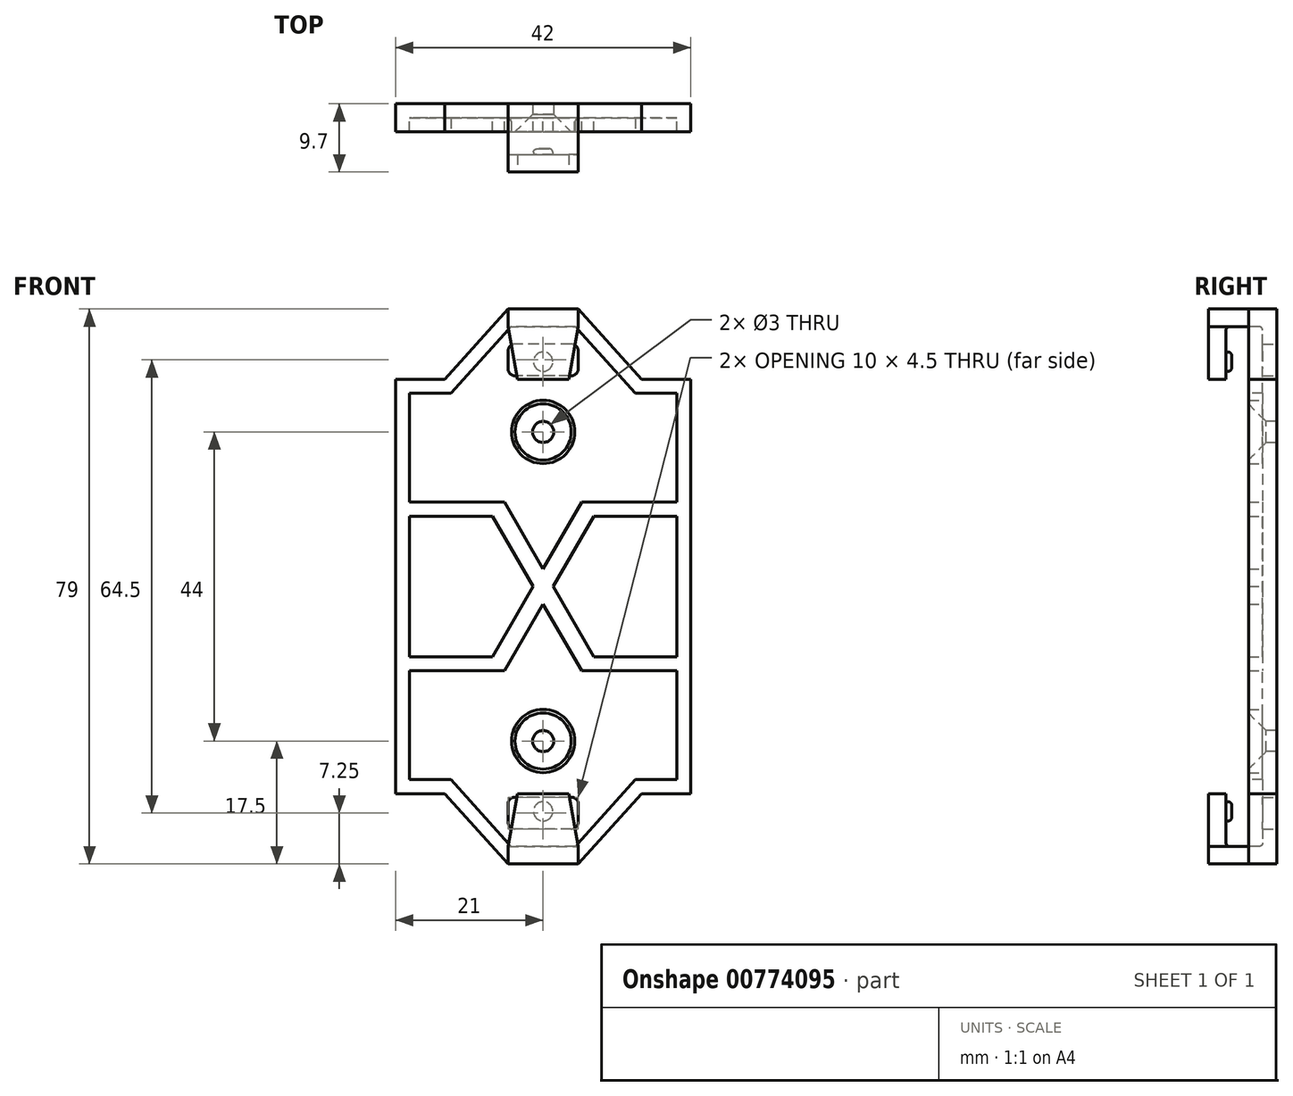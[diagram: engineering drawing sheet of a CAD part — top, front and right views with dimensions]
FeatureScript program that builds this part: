
annotation { "Feature Type Name" : "Feature", "Feature Type Description" : "" }
export const myFeature = defineFeature(function(context is Context, id is Id, definition is map)
    precondition{}
    {
        {
            var Q0;
            Q0=qCreatedBy(makeId("Front.planeOp"),FACE);
            var sketch = newSketch(context, id + "F0", { "sketchPlane" : qUnion([Q0])});
            skLineSegment(sketch, "E0.bottom", {"start": v(-21, 29.5) * mm, "end": v(-14, 29.5) * mm});
            skLineSegment(sketch, "E0.top", {"start": v(-21, -29.5) * mm, "end": v(-14, -29.5) * mm});
            skLineSegment(sketch, "E0.left", {"start": v(-21, 29.5) * mm, "end": v(-21, -29.5) * mm});
            skLineSegment(sketch, "E0.right", {"start": v(21, 29.5) * mm, "end": v(21, -29.5) * mm});
            skLineSegment(sketch, "E1", {"start": v(-14, 29.5) * mm, "end": v(-5, 39.5) * mm});
            skLineSegment(sketch, "E2", {"start": v(-5, 39.5) * mm, "end": v(5, 39.5) * mm});
            skLineSegment(sketch, "E3", {"start": v(5, 39.5) * mm, "end": v(14, 29.5) * mm});
            skLineSegment(sketch, "E4", {"start": v(0, 66.84) * mm, "end": v(0, -52.22) * mm, "construction": true});
            skLineSegment(sketch, "E5.trimOffspring", {"start": v(14, 29.5) * mm, "end": v(21, 29.5) * mm});
            skLineSegment(sketch, "E6", {"start": v(-14, -29.5) * mm, "end": v(-5, -39.5) * mm});
            skLineSegment(sketch, "E7", {"start": v(-5, -39.5) * mm, "end": v(5, -39.5) * mm});
            skLineSegment(sketch, "E8", {"start": v(5, -39.5) * mm, "end": v(14, -29.5) * mm});
            skLineSegment(sketch, "E9.trimOffspring", {"start": v(14, -29.5) * mm, "end": v(21, -29.5) * mm});
            skLineSegment(sketch, "E10", {"start": v(-46.22, 0) * mm, "end": v(54.83, 0) * mm, "construction": true});
            skSolve(sketch);
        }
        {
            var Q0;
            Q0 = qSketchRegion(id + "F0", true);
            extrude(context, id + "F1", {"entities" : qUnion([Q0]), "oppositeDirection" : true, "depth" : 4 * mm, "offsetDistance" : 25 * mm});
        }
        {
            var Q0;
            Q0=makeQuery(id+"F1.opExtrude","CAP_FACE",FACE,{"disambiguationData":[OSD([sQuery(id+"F0.wireOp",EDGE,"E0.bottom"),sQuery(id+"F0.wireOp",EDGE,"E0.top"),sQuery(id+"F0.wireOp",EDGE,"E0.left"),sQuery(id+"F0.wireOp",EDGE,"E0.right"),sQuery(id+"F0.wireOp",EDGE,"E1"),sQuery(id+"F0.wireOp",EDGE,"E2"),sQuery(id+"F0.wireOp",EDGE,"E3"),sQuery(id+"F0.wireOp",EDGE,"E5.trimOffspring"),sQuery(id+"F0.wireOp",EDGE,"E6"),sQuery(id+"F0.wireOp",EDGE,"E7"),sQuery(id+"F0.wireOp",EDGE,"E8"),sQuery(id+"F0.wireOp",EDGE,"E9.trimOffspring")])],"isStart":true});
            var sketch = newSketch(context, id + "F2", { "sketchPlane" : qUnion([Q0])});
            skLineSegment(sketch, "E11.0", {"start": v(-5, 39.5) * mm, "end": v(5, 39.5) * mm});
            skLineSegment(sketch, "E12", {"start": v(-5, 39.5) * mm, "end": v(-5, 37) * mm});
            skLineSegment(sketch, "E13", {"start": v(-5, 37) * mm, "end": v(5, 37) * mm});
            skLineSegment(sketch, "E14", {"start": v(5, 37) * mm, "end": v(5, 39.5) * mm});
            skLineSegment(sketch, "E15.0", {"start": v(-5, -39.5) * mm, "end": v(5, -39.5) * mm});
            skLineSegment(sketch, "E16", {"start": v(-5, -39.5) * mm, "end": v(-5, -37) * mm});
            skLineSegment(sketch, "E17", {"start": v(-5, -37) * mm, "end": v(5, -37) * mm});
            skLineSegment(sketch, "E18", {"start": v(5, -37) * mm, "end": v(5, -39.5) * mm});
            skSolve(sketch);
        }
        {
            var Q0;
            Q0 = qSketchRegion(id + "F2", true);
            extrude(context, id + "F3", {"entities" : qUnion([Q0]), "operationType" : NewBodyOperationType.ADD, "depth" : 5.7 * mm, "offsetDistance" : 25 * mm});
        }
        {
            var Q0;
            Q0=makeQuery(id+"F3.opExtrude","CAP_FACE",FACE,{"disambiguationData":[OSD([sQuery(id+"F2.wireOp",EDGE,"E11.0"),sQuery(id+"F2.wireOp",EDGE,"E12"),sQuery(id+"F2.wireOp",EDGE,"E13"),sQuery(id+"F2.wireOp",EDGE,"E14")])],"isStart":false});
            var sketch = newSketch(context, id + "F4", { "sketchPlane" : qUnion([Q0])});
            skLineSegment(sketch, "E19", {"start": v(-5, 39.5) * mm, "end": v(-5, 37) * mm});
            skLineSegment(sketch, "E20", {"start": v(-3.68, 29.5) * mm, "end": v(3.68, 29.5) * mm});
            skLineSegment(sketch, "E21", {"start": v(5, 37) * mm, "end": v(5, 39.5) * mm});
            skLineSegment(sketch, "E22", {"start": v(5, 39.5) * mm, "end": v(-5, 39.5) * mm});
            skLineSegment(sketch, "E23", {"start": v(-3.68, -29.5) * mm, "end": v(3.68, -29.5) * mm});
            skLineSegment(sketch, "E24", {"start": v(5, -37) * mm, "end": v(5, -39.5) * mm});
            skLineSegment(sketch, "E25", {"start": v(5, -39.5) * mm, "end": v(-5, -39.5) * mm});
            skLineSegment(sketch, "E26", {"start": v(-5, -39.5) * mm, "end": v(-5, -37) * mm});
            skLineSegment(sketch, "E27", {"start": v(5, -37) * mm, "end": v(3.68, -29.5) * mm});
            skLineSegment(sketch, "E28", {"start": v(-5, -37) * mm, "end": v(-3.68, -29.5) * mm});
            skPoint(sketch, "E29.0.end.orphan", {"position": v(5, -37) * mm});
            skLineSegment(sketch, "E30", {"start": v(5, 37) * mm, "end": v(3.68, 29.5) * mm});
            skLineSegment(sketch, "E31", {"start": v(-5, 37) * mm, "end": v(-3.68, 29.5) * mm});
            skSolve(sketch);
        }
        {
            var Q0;
            Q0 = qSketchRegion(id + "F4", true);
            extrude(context, id + "F5", {"entities" : qUnion([Q0]), "operationType" : NewBodyOperationType.ADD, "oppositeDirection" : true, "depth" : 2.5 * mm, "offsetDistance" : 25 * mm});
        }
        {
            var Q0;
            Q0=makeQuery(id+"F1.opExtrude","CAP_FACE",FACE,{"disambiguationData":[OSD([sQuery(id+"F0.wireOp",EDGE,"E0.bottom"),sQuery(id+"F0.wireOp",EDGE,"E0.top"),sQuery(id+"F0.wireOp",EDGE,"E0.left"),sQuery(id+"F0.wireOp",EDGE,"E0.right"),sQuery(id+"F0.wireOp",EDGE,"E1"),sQuery(id+"F0.wireOp",EDGE,"E2"),sQuery(id+"F0.wireOp",EDGE,"E3"),sQuery(id+"F0.wireOp",EDGE,"E5.trimOffspring"),sQuery(id+"F0.wireOp",EDGE,"E6"),sQuery(id+"F0.wireOp",EDGE,"E7"),sQuery(id+"F0.wireOp",EDGE,"E8"),sQuery(id+"F0.wireOp",EDGE,"E9.trimOffspring")])],"isStart":true});
            var sketch = newSketch(context, id + "F6", { "sketchPlane" : qUnion([Q0])});
            skCircle(sketch, "E32", {"center": v(0, 22) * mm, "radius": 1.5 * mm});
            skCircle(sketch, "E33", {"center": v(0, -22) * mm, "radius": 1.5 * mm});
            skLineSegment(sketch, "E34", {"start": v(19.03, 0) * mm, "end": v(-18.19, 0) * mm, "construction": true});
            skSolve(sketch);
        }
        {
            var Q0;
            Q0 = qSketchRegion(id + "F6", true);
            extrude(context, id + "F7", {"entities" : qUnion([Q0]), "operationType" : NewBodyOperationType.REMOVE, "endBound" : BoundingType.UP_TO_NEXT, "oppositeDirection" : true, "depth" : 25 * mm, "offsetDistance" : 25 * mm});
        }
        {
            var Q0;
            Q0=makeQuery(id+"F1.opExtrude","CAP_FACE",FACE,{"disambiguationData":[OSD([sQuery(id+"F0.wireOp",EDGE,"E0.bottom"),sQuery(id+"F0.wireOp",EDGE,"E0.top"),sQuery(id+"F0.wireOp",EDGE,"E0.left"),sQuery(id+"F0.wireOp",EDGE,"E0.right"),sQuery(id+"F0.wireOp",EDGE,"E1"),sQuery(id+"F0.wireOp",EDGE,"E2"),sQuery(id+"F0.wireOp",EDGE,"E3"),sQuery(id+"F0.wireOp",EDGE,"E5.trimOffspring"),sQuery(id+"F0.wireOp",EDGE,"E6"),sQuery(id+"F0.wireOp",EDGE,"E7"),sQuery(id+"F0.wireOp",EDGE,"E8"),sQuery(id+"F0.wireOp",EDGE,"E9.trimOffspring")])],"isStart":true});
            var sketch = newSketch(context, id + "F8", { "sketchPlane" : qUnion([Q0])});
            skLineSegment(sketch, "E35.0", {"start": v(-13.1, -27.5) * mm, "end": v(-6.36, -35) * mm});
            skLineSegment(sketch, "E35.1", {"start": v(19, 27.5) * mm, "end": v(13.1, 27.5) * mm});
            skLineSegment(sketch, "E35.2", {"start": v(19, -27.5) * mm, "end": v(19, 27.5) * mm});
            skLineSegment(sketch, "E35.3", {"start": v(13.1, -27.5) * mm, "end": v(19, -27.5) * mm});
            skLineSegment(sketch, "E35.4", {"start": v(6.36, -35) * mm, "end": v(13.1, -27.5) * mm});
            skLineSegment(sketch, "E35.5", {"start": v(13.1, 27.5) * mm, "end": v(6.36, 35) * mm});
            skLineSegment(sketch, "E35.6", {"start": v(-6.36, -35) * mm, "end": v(6.36, -35) * mm});
            skLineSegment(sketch, "E35.7", {"start": v(6.36, 35) * mm, "end": v(-6.36, 35) * mm});
            skLineSegment(sketch, "E35.8", {"start": v(-6.36, 35) * mm, "end": v(-13.1, 27.5) * mm});
            skLineSegment(sketch, "E35.9", {"start": v(-13.1, 27.5) * mm, "end": v(-19, 27.5) * mm});
            skLineSegment(sketch, "E35.10", {"start": v(-19, 27.5) * mm, "end": v(-19, -27.5) * mm});
            skLineSegment(sketch, "E35.11", {"start": v(-19, -27.5) * mm, "end": v(-13.1, -27.5) * mm});
            skSolve(sketch);
        }
        {
            var Q0;
            Q0 = qSketchRegion(id + "F8", true);
            extrude(context, id + "F9", {"entities" : qUnion([Q0]), "operationType" : NewBodyOperationType.REMOVE, "oppositeDirection" : true, "depth" : 2 * mm, "offsetDistance" : 25 * mm});
        }
        {
            var Q0;
            Q0=makeQuery(id+"F9.boolean.opBoolean","COPY",FACE,{"derivedFrom":makeQuery(id+"F9.opExtrude","CAP_FACE",FACE,{"disambiguationData":[OSD([sQuery(id+"F8.wireOp",EDGE,"E35.0"),sQuery(id+"F8.wireOp",EDGE,"E35.1"),sQuery(id+"F8.wireOp",EDGE,"E35.2"),sQuery(id+"F8.wireOp",EDGE,"E35.3"),sQuery(id+"F8.wireOp",EDGE,"E35.4"),sQuery(id+"F8.wireOp",EDGE,"E35.5"),sQuery(id+"F8.wireOp",EDGE,"E35.6"),sQuery(id+"F8.wireOp",EDGE,"E35.7"),sQuery(id+"F8.wireOp",EDGE,"E35.8"),sQuery(id+"F8.wireOp",EDGE,"E35.9"),sQuery(id+"F8.wireOp",EDGE,"E35.10"),sQuery(id+"F8.wireOp",EDGE,"E35.11")])],"isStart":false})});
            var sketch = newSketch(context, id + "F10", { "sketchPlane" : qUnion([Q0])});
            skCircle(sketch, "E36.0", {"center": v(0, -22) * mm, "radius": 1.5 * mm});
            skCircle(sketch, "E37", {"center": v(0, -22) * mm, "radius": 4.5 * mm});
            skCircle(sketch, "E38.0", {"center": v(0, 22) * mm, "radius": 1.5 * mm});
            skCircle(sketch, "E39", {"center": v(0, 22) * mm, "radius": 4.5 * mm});
            skSolve(sketch);
        }
        {
            var Q0;
            Q0 = qSketchRegion(id + "F10", true);
            var Q1;
            Q1=makeQuery(id+"F1.opExtrude","CAP_FACE",FACE,{"disambiguationData":[OSD([sQuery(id+"F0.wireOp",EDGE,"E0.bottom"),sQuery(id+"F0.wireOp",EDGE,"E0.top"),sQuery(id+"F0.wireOp",EDGE,"E0.left"),sQuery(id+"F0.wireOp",EDGE,"E0.right"),sQuery(id+"F0.wireOp",EDGE,"E1"),sQuery(id+"F0.wireOp",EDGE,"E2"),sQuery(id+"F0.wireOp",EDGE,"E3"),sQuery(id+"F0.wireOp",EDGE,"E5.trimOffspring"),sQuery(id+"F0.wireOp",EDGE,"E6"),sQuery(id+"F0.wireOp",EDGE,"E7"),sQuery(id+"F0.wireOp",EDGE,"E8"),sQuery(id+"F0.wireOp",EDGE,"E9.trimOffspring")])],"isStart":true});
            extrude(context, id + "F11", {"entities" : qUnion([Q0]), "operationType" : NewBodyOperationType.ADD, "endBound" : BoundingType.UP_TO_SURFACE, "depth" : 25 * mm, "endBoundEntityFace" : qUnion([Q1]), "offsetDistance" : 25 * mm});
        }
        {
            var Q0;
            Q0=makeQuery(id+"F1.opExtrude","CAP_FACE",FACE,{"disambiguationData":[OSD([sQuery(id+"F0.wireOp",EDGE,"E0.bottom"),sQuery(id+"F0.wireOp",EDGE,"E0.top"),sQuery(id+"F0.wireOp",EDGE,"E0.left"),sQuery(id+"F0.wireOp",EDGE,"E0.right"),sQuery(id+"F0.wireOp",EDGE,"E1"),sQuery(id+"F0.wireOp",EDGE,"E2"),sQuery(id+"F0.wireOp",EDGE,"E3"),sQuery(id+"F0.wireOp",EDGE,"E5.trimOffspring"),sQuery(id+"F0.wireOp",EDGE,"E6"),sQuery(id+"F0.wireOp",EDGE,"E7"),sQuery(id+"F0.wireOp",EDGE,"E8"),sQuery(id+"F0.wireOp",EDGE,"E9.trimOffspring")])],"isStart":true});
            var sketch = newSketch(context, id + "F12", { "sketchPlane" : qUnion([Q0])});
            skLineSegment(sketch, "E40", {"start": v(4.56, -37) * mm, "end": v(-4.56, -37) * mm});
            skLineSegment(sketch, "E41", {"start": v(-5, -35) * mm, "end": v(5, -35) * mm});
            skLineSegment(sketch, "E42", {"start": v(-4.56, 37) * mm, "end": v(4.56, 37) * mm});
            skLineSegment(sketch, "E43", {"start": v(-6.36, 35) * mm, "end": v(-4.56, 37) * mm});
            skLineSegment(sketch, "E44", {"start": v(6.36, 35) * mm, "end": v(4.56, 37) * mm});
            skPoint(sketch, "E45.orphan", {"position": v(5, 35) * mm});
            skLineSegment(sketch, "E46", {"start": v(-6.36, 35) * mm, "end": v(6.36, 35) * mm});
            skLineSegment(sketch, "E47", {"start": v(6.36, -35) * mm, "end": v(4.56, -37) * mm});
            skLineSegment(sketch, "E48", {"start": v(-6.36, -35) * mm, "end": v(-4.56, -37) * mm});
            skLineSegment(sketch, "E49", {"start": v(-6.36, -35) * mm, "end": v(6.36, -35) * mm});
            skPoint(sketch, "E50.orphan", {"position": v(5, -37) * mm});
            skSolve(sketch);
        }
        {
            var Q0;
            Q0 = qSketchRegion(id + "F12", true);
            var Q1;
            Q1=makeQuery(id+"F9.boolean.opBoolean","COPY",FACE,{"derivedFrom":makeQuery(id+"F9.opExtrude","CAP_FACE",FACE,{"disambiguationData":[OSD([sQuery(id+"F8.wireOp",EDGE,"E35.0"),sQuery(id+"F8.wireOp",EDGE,"E35.1"),sQuery(id+"F8.wireOp",EDGE,"E35.2"),sQuery(id+"F8.wireOp",EDGE,"E35.3"),sQuery(id+"F8.wireOp",EDGE,"E35.4"),sQuery(id+"F8.wireOp",EDGE,"E35.5"),sQuery(id+"F8.wireOp",EDGE,"E35.6"),sQuery(id+"F8.wireOp",EDGE,"E35.7"),sQuery(id+"F8.wireOp",EDGE,"E35.8"),sQuery(id+"F8.wireOp",EDGE,"E35.9"),sQuery(id+"F8.wireOp",EDGE,"E35.10"),sQuery(id+"F8.wireOp",EDGE,"E35.11")])],"isStart":false})});
            extrude(context, id + "F13", {"entities" : qUnion([Q0]), "operationType" : NewBodyOperationType.REMOVE, "endBound" : BoundingType.UP_TO_SURFACE, "oppositeDirection" : true, "depth" : 25 * mm, "endBoundEntityFace" : qUnion([Q1]), "offsetDistance" : 25 * mm});
        }
        {
            var Q0;
            Q0=makeQuery(id+"F13.boolean.opBoolean","MERGE",FACE,{"derivedFrom":[makeQuery(id+"F9.boolean.opBoolean","COPY",FACE,{"derivedFrom":makeQuery(id+"F9.opExtrude","CAP_FACE",FACE,{"disambiguationData":[OSD([sQuery(id+"F8.wireOp",EDGE,"E35.0"),sQuery(id+"F8.wireOp",EDGE,"E35.1"),sQuery(id+"F8.wireOp",EDGE,"E35.2"),sQuery(id+"F8.wireOp",EDGE,"E35.3"),sQuery(id+"F8.wireOp",EDGE,"E35.4"),sQuery(id+"F8.wireOp",EDGE,"E35.5"),sQuery(id+"F8.wireOp",EDGE,"E35.6"),sQuery(id+"F8.wireOp",EDGE,"E35.7"),sQuery(id+"F8.wireOp",EDGE,"E35.8"),sQuery(id+"F8.wireOp",EDGE,"E35.9"),sQuery(id+"F8.wireOp",EDGE,"E35.10"),sQuery(id+"F8.wireOp",EDGE,"E35.11")])],"isStart":false})})],"fromTools":[makeQuery(id+"F13.opExtrude","CAP_FACE",FACE,{"disambiguationData":[OSD([sQuery(id+"F12.wireOp",EDGE,"E40"),sQuery(id+"F12.wireOp",EDGE,"E47"),sQuery(id+"F12.wireOp",EDGE,"E48"),sQuery(id+"F12.wireOp",EDGE,"E49")])],"isStart":false}),makeQuery(id+"F13.opExtrude","CAP_FACE",FACE,{"disambiguationData":[OSD([sQuery(id+"F12.wireOp",EDGE,"E42"),sQuery(id+"F12.wireOp",EDGE,"E43"),sQuery(id+"F12.wireOp",EDGE,"E44"),sQuery(id+"F12.wireOp",EDGE,"E46")])],"isStart":false})]});
            var sketch = newSketch(context, id + "F14", { "sketchPlane" : qUnion([Q0])});
            skLineSegment(sketch, "E51.bottom", {"start": v(19, -12) * mm, "end": v(5.48, -12) * mm});
            skLineSegment(sketch, "E51.top", {"start": v(19, -10) * mm, "end": v(7.22, -10) * mm});
            skLineSegment(sketch, "E51.left", {"start": v(19, -12) * mm, "end": v(19, -10) * mm});
            skLineSegment(sketch, "E51.right", {"start": v(-19, -12) * mm, "end": v(-19, -10) * mm});
            skLineSegment(sketch, "E52.bottom", {"start": v(19, 10) * mm, "end": v(7.22, 10) * mm});
            skLineSegment(sketch, "E52.top", {"start": v(19, 12) * mm, "end": v(5.48, 12) * mm});
            skLineSegment(sketch, "E52.left", {"start": v(19, 10) * mm, "end": v(19, 12) * mm});
            skLineSegment(sketch, "E52.right", {"start": v(-19, 10) * mm, "end": v(-19, 12) * mm});
            skLineSegment(sketch, "E53", {"start": v(-7.22, 10) * mm, "end": v(-1.44, 0) * mm});
            skLineSegment(sketch, "E54", {"start": v(-5.48, 12) * mm, "end": v(0, 2.5) * mm});
            skLineSegment(sketch, "E55", {"start": v(-18.6, 32.21) * mm, "end": v(23.82, -41.26) * mm, "construction": true});
            skLineSegment(sketch, "E56", {"start": v(27.25, 47.2) * mm, "end": v(-33.95, -58.8) * mm, "construction": true});
            skLineSegment(sketch, "E57", {"start": v(5.48, 12) * mm, "end": v(0, 2.5) * mm});
            skLineSegment(sketch, "E58.trimOffspring", {"start": v(-7.22, 10) * mm, "end": v(-19, 10) * mm});
            skLineSegment(sketch, "E59.trimOffspring", {"start": v(-5.48, 12) * mm, "end": v(-19, 12) * mm});
            skLineSegment(sketch, "E60.trimOffspring", {"start": v(7.22, 10) * mm, "end": v(1.44, 0) * mm});
            skLineSegment(sketch, "E61.trimOffspring", {"start": v(-7.22, -10) * mm, "end": v(-19, -10) * mm});
            skLineSegment(sketch, "E62.trimOffspring", {"start": v(-5.48, -12) * mm, "end": v(-19, -12) * mm});
            skLineSegment(sketch, "E63.trimOffspring", {"start": v(-1.44, 0) * mm, "end": v(-7.22, -10) * mm});
            skLineSegment(sketch, "E64.trimOffspring", {"start": v(0, -2.5) * mm, "end": v(5.48, -12) * mm});
            skLineSegment(sketch, "E65.trimOffspring", {"start": v(0, -2.5) * mm, "end": v(-5.48, -12) * mm});
            skLineSegment(sketch, "E66.trimOffspring", {"start": v(1.44, 0) * mm, "end": v(7.22, -10) * mm});
            skSolve(sketch);
        }
        {
            var Q0;
            Q0 = qSketchRegion(id + "F14", true);
            var Q1;
            {var subQ0=sQuery(id+"F0.wireOp",EDGE,"E0.left");var subQ1=sQuery(id+"F0.wireOp",EDGE,"E6");var subQ2=sQuery(id+"F0.wireOp",EDGE,"E2");var subQ3=sQuery(id+"F0.wireOp",EDGE,"E7");var subQ4=sQuery(id+"F0.wireOp",EDGE,"E0.bottom");var subQ5=sQuery(id+"F0.wireOp",EDGE,"E0.top");var subQ6=sQuery(id+"F0.wireOp",EDGE,"E1");Q1=makeQuery(id+"F13.boolean.opBoolean","SPLIT",FACE,{"disambiguationData":[TD([makeQuery(id+"F1.opExtrude","SWEPT_FACE",FACE,{"disambiguationData":[OSD([subQ4])]})])],"derivedFrom":makeQuery(id+"F1.opExtrude","CAP_FACE",FACE,{"disambiguationData":[OSD([subQ4,subQ5,subQ0,sQuery(id+"F0.wireOp",EDGE,"E0.right"),subQ6,subQ2,sQuery(id+"F0.wireOp",EDGE,"E3"),sQuery(id+"F0.wireOp",EDGE,"E5.trimOffspring"),subQ1,subQ3,sQuery(id+"F0.wireOp",EDGE,"E8"),sQuery(id+"F0.wireOp",EDGE,"E9.trimOffspring")])],"isStart":true})});}
            extrude(context, id + "F15", {"entities" : qUnion([Q0]), "operationType" : NewBodyOperationType.ADD, "endBound" : BoundingType.UP_TO_SURFACE, "depth" : 25 * mm, "endBoundEntityFace" : qUnion([Q1]), "offsetDistance" : 25 * mm});
        }
        {
            var Q0;
            Q0=makeQuery(id+"F5.opExtrude","CAP_FACE",FACE,{"disambiguationData":[OSD([sQuery(id+"F4.wireOp",EDGE,"E19"),sQuery(id+"F4.wireOp",EDGE,"E20"),sQuery(id+"F4.wireOp",EDGE,"E21"),sQuery(id+"F4.wireOp",EDGE,"E22")])],"isStart":false});
            var sketch = newSketch(context, id + "F16", { "sketchPlane" : qUnion([Q0])});
            skLineSegment(sketch, "E67", {"start": v(0, -39.62) * mm, "end": v(0, 39.43) * mm, "construction": true});
            skCircle(sketch, "E68", {"center": v(0, -32) * mm, "radius": 1.38 * mm});
            skCircle(sketch, "E69", {"center": v(0, 32) * mm, "radius": 1.38 * mm});
            skSolve(sketch);
        }
        {
            var Q0;
            Q0 = qSketchRegion(id + "F16", true);
            extrude(context, id + "F17", {"entities" : qUnion([Q0]), "operationType" : NewBodyOperationType.ADD, "depth" : 0.8 * mm, "offsetDistance" : 25 * mm});
        }
        {
            var Q0;
            Q0=makeQuery(id+"F11.opExtrude","CAP_EDGE",EDGE,{"disambiguationData":[OSD([sQuery(id+"F10.wireOp",EDGE,"E36.0")])],"isStart":false});
            var Q1;
            Q1=makeQuery(id+"F11.opExtrude","CAP_EDGE",EDGE,{"disambiguationData":[OSD([sQuery(id+"F10.wireOp",EDGE,"E38.0")])],"isStart":false});
            chamfer(context, id + "F18", {"entities" : qUnion([Q0, Q1]), "width" : 2.5 * mm, "tangentPropagation" : true});
        }
        {
            var Q0;
            Q0=makeQuery(id+"F1.opExtrude","CAP_FACE",FACE,{"disambiguationData":[OSD([sQuery(id+"F0.wireOp",EDGE,"E0.bottom"),sQuery(id+"F0.wireOp",EDGE,"E0.top"),sQuery(id+"F0.wireOp",EDGE,"E0.left"),sQuery(id+"F0.wireOp",EDGE,"E0.right"),sQuery(id+"F0.wireOp",EDGE,"E1"),sQuery(id+"F0.wireOp",EDGE,"E2"),sQuery(id+"F0.wireOp",EDGE,"E3"),sQuery(id+"F0.wireOp",EDGE,"E5.trimOffspring"),sQuery(id+"F0.wireOp",EDGE,"E6"),sQuery(id+"F0.wireOp",EDGE,"E7"),sQuery(id+"F0.wireOp",EDGE,"E8"),sQuery(id+"F0.wireOp",EDGE,"E9.trimOffspring")])],"isStart":false});
            var sketch = newSketch(context, id + "F19", { "sketchPlane" : qUnion([Q0])});
            skLineSegment(sketch, "E70.bottom", {"start": v(-5, 34.5) * mm, "end": v(5, 34.5) * mm});
            skLineSegment(sketch, "E70.top", {"start": v(-5, 30) * mm, "end": v(5, 30) * mm});
            skLineSegment(sketch, "E70.left", {"start": v(-5, 34.5) * mm, "end": v(-5, 30) * mm});
            skLineSegment(sketch, "E70.right", {"start": v(5, 34.5) * mm, "end": v(5, 30) * mm});
            skLineSegment(sketch, "E71", {"start": v(0, 42.26) * mm, "end": v(0, -49.3) * mm, "construction": true});
            skLineSegment(sketch, "E72.bottom", {"start": v(-5, -30) * mm, "end": v(5, -30) * mm});
            skLineSegment(sketch, "E72.top", {"start": v(-5, -34.5) * mm, "end": v(5, -34.5) * mm});
            skLineSegment(sketch, "E72.left", {"start": v(-5, -30) * mm, "end": v(-5, -34.5) * mm});
            skLineSegment(sketch, "E72.right", {"start": v(5, -30) * mm, "end": v(5, -34.5) * mm});
            skSolve(sketch);
        }
        {
            var Q0;
            Q0 = qSketchRegion(id + "F19", true);
            extrude(context, id + "F20", {"entities" : qUnion([Q0]), "operationType" : NewBodyOperationType.REMOVE, "endBound" : BoundingType.UP_TO_NEXT, "oppositeDirection" : true, "depth" : 25 * mm, "offsetDistance" : 25 * mm});
        }
        {
            var Q0;
            Q0=makeQuery(id+"F20.boolean.opBoolean","COPY",EDGE,{"derivedFrom":makeQuery(id+"F20.opExtrude","SWEPT_EDGE",EDGE,{"disambiguationData":[OSD([sQuery(id+"F19.wireOp",EDGE,"E70.bottom"),sQuery(id+"F19.wireOp",EDGE,"E70.right")])]})});
            var Q1;
            Q1=makeQuery(id+"F20.boolean.opBoolean","COPY",EDGE,{"derivedFrom":makeQuery(id+"F20.opExtrude","SWEPT_EDGE",EDGE,{"disambiguationData":[OSD([sQuery(id+"F19.wireOp",EDGE,"E70.top"),sQuery(id+"F19.wireOp",EDGE,"E70.left")])]})});
            var Q2;
            Q2=makeQuery(id+"F20.boolean.opBoolean","COPY",EDGE,{"derivedFrom":makeQuery(id+"F20.opExtrude","SWEPT_EDGE",EDGE,{"disambiguationData":[OSD([sQuery(id+"F19.wireOp",EDGE,"E70.bottom"),sQuery(id+"F19.wireOp",EDGE,"E70.left")])]})});
            var Q3;
            Q3=makeQuery(id+"F20.boolean.opBoolean","COPY",EDGE,{"derivedFrom":makeQuery(id+"F20.opExtrude","SWEPT_EDGE",EDGE,{"disambiguationData":[OSD([sQuery(id+"F19.wireOp",EDGE,"E70.top"),sQuery(id+"F19.wireOp",EDGE,"E70.right")])]})});
            var Q4;
            Q4=makeQuery(id+"F20.boolean.opBoolean","COPY",EDGE,{"derivedFrom":makeQuery(id+"F20.opExtrude","SWEPT_EDGE",EDGE,{"disambiguationData":[OSD([sQuery(id+"F19.wireOp",EDGE,"E72.top"),sQuery(id+"F19.wireOp",EDGE,"E72.left")])]})});
            var Q5;
            Q5=makeQuery(id+"F20.boolean.opBoolean","COPY",EDGE,{"derivedFrom":makeQuery(id+"F20.opExtrude","SWEPT_EDGE",EDGE,{"disambiguationData":[OSD([sQuery(id+"F19.wireOp",EDGE,"E72.bottom"),sQuery(id+"F19.wireOp",EDGE,"E72.left")])]})});
            var Q6;
            Q6=makeQuery(id+"F20.boolean.opBoolean","COPY",EDGE,{"derivedFrom":makeQuery(id+"F20.opExtrude","SWEPT_EDGE",EDGE,{"disambiguationData":[OSD([sQuery(id+"F19.wireOp",EDGE,"E72.bottom"),sQuery(id+"F19.wireOp",EDGE,"E72.right")])]})});
            var Q7;
            Q7=makeQuery(id+"F20.boolean.opBoolean","COPY",EDGE,{"derivedFrom":makeQuery(id+"F20.opExtrude","SWEPT_EDGE",EDGE,{"disambiguationData":[OSD([sQuery(id+"F19.wireOp",EDGE,"E72.top"),sQuery(id+"F19.wireOp",EDGE,"E72.right")])]})});
            fillet(context, id + "F21", {"entities" : qUnion([Q0, Q1, Q2, Q3, Q4, Q5, Q6, Q7]), "radius" : 1 * mm, "tangentPropagation" : true, "allowEdgeOverflow" : false});
        }
        {
            var Q0;
            Q0=makeQuery(id+"F17.opExtrude","CAP_EDGE",EDGE,{"disambiguationData":[OSD([sQuery(id+"F16.wireOp",EDGE,"E68")])],"isStart":false});
            var Q1;
            Q1=makeQuery(id+"F17.opExtrude","CAP_EDGE",EDGE,{"disambiguationData":[OSD([sQuery(id+"F16.wireOp",EDGE,"E69")])],"isStart":false});
            fillet(context, id + "F22", {"entities" : qUnion([Q0, Q1]), "radius" : 0.5 * mm, "tangentPropagation" : true, "allowEdgeOverflow" : false});
        }
        {
            var Q0;
            Q0=makeQuery(id+"F13.boolean.opBoolean","COPY",EDGE,{"derivedFrom":makeQuery(id+"F13.opExtrude","CAP_EDGE",EDGE,{"disambiguationData":[OSD([sQuery(id+"F12.wireOp",EDGE,"E42")])],"isStart":false})});
            var Q1;
            Q1=makeQuery(id+"F13.boolean.opBoolean","COPY",EDGE,{"derivedFrom":makeQuery(id+"F13.opExtrude","CAP_EDGE",EDGE,{"disambiguationData":[OSD([sQuery(id+"F12.wireOp",EDGE,"E40")])],"isStart":false})});
            var Q2;
            Q2=makeQuery(id+"F5.boolean.opBoolean","INTERSECT",EDGE,{"derivedFrom":[makeQuery(id+"F3.opExtrude","SWEPT_FACE",FACE,{"disambiguationData":[OSD([sQuery(id+"F2.wireOp",EDGE,"E13")])]}),makeQuery(id+"F5.opExtrude","CAP_FACE",FACE,{"disambiguationData":[OSD([sQuery(id+"F4.wireOp",EDGE,"E19"),sQuery(id+"F4.wireOp",EDGE,"E20"),sQuery(id+"F4.wireOp",EDGE,"E21"),sQuery(id+"F4.wireOp",EDGE,"E22"),sQuery(id+"F4.wireOp",EDGE,"E30"),sQuery(id+"F4.wireOp",EDGE,"E31")])],"isStart":false})]});
            var Q3;
            Q3=makeQuery(id+"F5.boolean.opBoolean","INTERSECT",EDGE,{"derivedFrom":[makeQuery(id+"F3.opExtrude","SWEPT_FACE",FACE,{"disambiguationData":[OSD([sQuery(id+"F2.wireOp",EDGE,"E17")])]}),makeQuery(id+"F5.opExtrude","CAP_FACE",FACE,{"disambiguationData":[OSD([sQuery(id+"F4.wireOp",EDGE,"E23"),sQuery(id+"F4.wireOp",EDGE,"E24"),sQuery(id+"F4.wireOp",EDGE,"E25"),sQuery(id+"F4.wireOp",EDGE,"E26"),sQuery(id+"F4.wireOp",EDGE,"E27"),sQuery(id+"F4.wireOp",EDGE,"E28")])],"isStart":false})]});
            fillet(context, id + "F23", {"entities" : qUnion([Q0, Q1, Q2, Q3]), "radius" : 0.5 * mm, "tangentPropagation" : true, "allowEdgeOverflow" : false});
        }
    });
